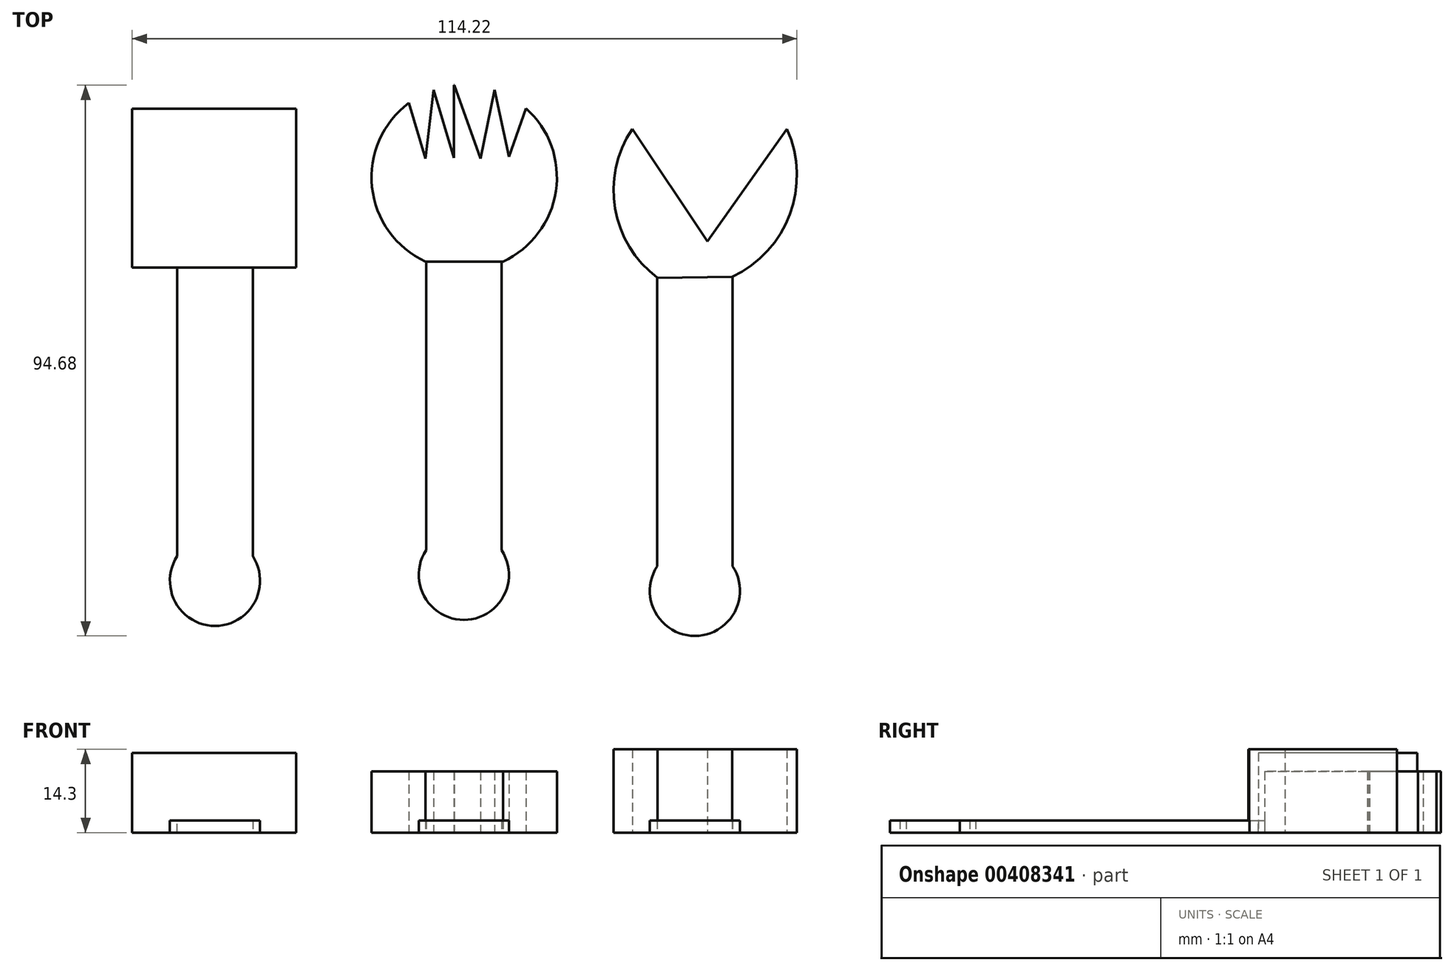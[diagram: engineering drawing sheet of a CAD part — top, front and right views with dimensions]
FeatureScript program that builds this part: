
annotation { "Feature Type Name" : "Feature", "Feature Type Description" : "" }
export const myFeature = defineFeature(function(context is Context, id is Id, definition is map)
    precondition{}
    {
        {
            var Q0;
            Q0=qCreatedBy(makeId("Top.planeOp"),FACE);
            var sketch = newSketch(context, id + "F0", { "sketchPlane" : qUnion([Q0])});
            skArc(sketch, "E0", {"start": v(-4.8, -17.78) * mm, "mid": v(1.69, -29.76) * mm, "end": v(8.18, -17.78) * mm});
            skLineSegment(sketch, "E1", {"start": v(-4.8, -17.78) * mm, "end": v(-4.8, 32) * mm});
            skLineSegment(sketch, "E2", {"start": v(8.18, -17.78) * mm, "end": v(8.18, 32) * mm});
            skLineSegment(sketch, "E3", {"start": v(-4.8, 32) * mm, "end": v(8.18, 32) * mm});
            skSolve(sketch);
        }
        {
            var Q0;
            Q0 = qSketchRegion(id + "F0", true);
            extrude(context, id + "F1", {"entities" : qUnion([Q0]), "depth" : 2.1 * mm});
        }
        {
            var Q0;
            Q0=qCreatedBy(makeId("Top.planeOp"),FACE);
            var sketch = newSketch(context, id + "F2", { "sketchPlane" : qUnion([Q0])});
            skArc(sketch, "E4", {"start": v(-47.56, -18.81) * mm, "mid": v(-41.07, -30.8) * mm, "end": v(-34.58, -18.81) * mm});
            skLineSegment(sketch, "E5", {"start": v(-47.56, -18.81) * mm, "end": v(-47.56, 30.97) * mm});
            skLineSegment(sketch, "E6", {"start": v(-34.58, -18.81) * mm, "end": v(-34.58, 30.97) * mm});
            skLineSegment(sketch, "E7", {"start": v(-47.56, 30.97) * mm, "end": v(-34.58, 30.97) * mm});
            skSolve(sketch);
        }
        {
            var Q0;
            Q0 = qSketchRegion(id + "F2", true);
            extrude(context, id + "F3", {"entities" : qUnion([Q0]), "depth" : 2.1 * mm});
        }
        {
            var Q0;
            Q0=qCreatedBy(makeId("Top.planeOp"),FACE);
            var sketch = newSketch(context, id + "F4", { "sketchPlane" : qUnion([Q0])});
            skArc(sketch, "E8", {"start": v(34.91, -20.54) * mm, "mid": v(41.4, -32.52) * mm, "end": v(47.89, -20.54) * mm});
            skLineSegment(sketch, "E9", {"start": v(34.91, -20.54) * mm, "end": v(34.91, 29.25) * mm});
            skLineSegment(sketch, "E10", {"start": v(47.89, -20.54) * mm, "end": v(47.89, 29.25) * mm});
            skLineSegment(sketch, "E11", {"start": v(34.91, 29.25) * mm, "end": v(47.89, 29.25) * mm});
            skSolve(sketch);
        }
        {
            var Q0;
            Q0=qCreatedBy(makeId("Top.planeOp"),FACE);
            var sketch = newSketch(context, id + "F5", { "sketchPlane" : qUnion([Q0])});
            skArc(sketch, "E12", {"start": v(8.4, 31.85) * mm, "mid": v(1.75, 62.26) * mm, "end": v(-4.9, 31.85) * mm});
            skLineSegment(sketch, "E13", {"start": v(12.37, 58.2) * mm, "end": v(9.45, 49.88) * mm});
            skLineSegment(sketch, "E14", {"start": v(9.45, 49.88) * mm, "end": v(6.98, 61.37) * mm});
            skLineSegment(sketch, "E15", {"start": v(6.98, 61.37) * mm, "end": v(4.55, 49.53) * mm});
            skLineSegment(sketch, "E16", {"start": v(4.55, 49.53) * mm, "end": v(0, 62.26) * mm});
            skPoint(sketch, "E16.endSnap0", {"position": v(1.75, 62.26) * mm});
            skLineSegment(sketch, "E17", {"start": v(0, 62.26) * mm, "end": v(0, 49.7) * mm});
            skLineSegment(sketch, "E18", {"start": v(0, 49.7) * mm, "end": v(-3.48, 61.37) * mm});
            skLineSegment(sketch, "E19", {"start": v(-3.48, 61.37) * mm, "end": v(-4.9, 49.53) * mm});
            skLineSegment(sketch, "E20", {"start": v(-4.9, 49.53) * mm, "end": v(-7.76, 59.1) * mm});
            skLineSegment(sketch, "E21", {"start": v(-4.9, 31.85) * mm, "end": v(8.4, 31.85) * mm});
            skSolve(sketch);
        }
        {
            var Q0;
            Q0=qCreatedBy(makeId("Top.planeOp"),FACE);
            var sketch = newSketch(context, id + "F6", { "sketchPlane" : qUnion([Q0])});
            skLineSegment(sketch, "E22.bottom", {"start": v(-27.13, 58.1) * mm, "end": v(-55.3, 58.1) * mm});
            skLineSegment(sketch, "E22.top", {"start": v(-27.13, 30.8) * mm, "end": v(-55.3, 30.8) * mm});
            skLineSegment(sketch, "E22.left", {"start": v(-27.13, 58.1) * mm, "end": v(-27.13, 30.8) * mm});
            skLineSegment(sketch, "E22.right", {"start": v(-55.3, 58.1) * mm, "end": v(-55.3, 30.8) * mm});
            skSolve(sketch);
        }
        {
            var Q0;
            {var subQ8=sQuery(id+"F5.wireOp",EDGE,"E13");Q0=makeQuery(id+"F5.imprint","IMPRINT",FACE,{"disambiguationData":[TD([[makeQuery(id+"F5.imprint","IMPRINT",EDGE,{"derivedFrom":subQ8}),1.0]])]});}
            extrude(context, id + "F7", {"entities" : qUnion([Q0]), "operationType" : NewBodyOperationType.ADD, "depth" : 10.5 * mm});
        }
        {
            var Q0;
            Q0 = qSketchRegion(id + "F6", true);
            extrude(context, id + "F8", {"entities" : qUnion([Q0]), "operationType" : NewBodyOperationType.ADD, "depth" : 13.7 * mm});
        }
        {
            var Q0;
            Q0=makeQuery(id+"F4.imprint","IMPRINT",FACE,{"disambiguationData":[TD([[makeQuery(id+"F4.imprint","IMPRINT",EDGE,{"derivedFrom":sQuery(id+"F4.wireOp",EDGE,"E8")}),1.0]])]});
            extrude(context, id + "F9", {"entities" : qUnion([Q0]), "depth" : 2.1 * mm});
        }
        {
            var Q0;
            Q0=qCreatedBy(makeId("Top.planeOp"),FACE);
            var sketch = newSketch(context, id + "F10", { "sketchPlane" : qUnion([Q0])});
            skArc(sketch, "E23", {"start": v(30.63, 54.6) * mm, "mid": v(27.69, 40.95) * mm, "end": v(35, 29.05) * mm});
            skArc(sketch, "E24", {"start": v(47.78, 29.23) * mm, "mid": v(57.7, 39.97) * mm, "end": v(57.23, 54.6) * mm});
            skLineSegment(sketch, "E25", {"start": v(57.23, 54.6) * mm, "end": v(43.58, 35.35) * mm});
            skLineSegment(sketch, "E26", {"start": v(43.58, 35.35) * mm, "end": v(30.63, 54.6) * mm});
            skLineSegment(sketch, "E27", {"start": v(35, 29.05) * mm, "end": v(47.78, 29.23) * mm});
            skSolve(sketch);
        }
        {
            var Q0;
            Q0 = qSketchRegion(id + "F10", true);
            extrude(context, id + "F11", {"entities" : qUnion([Q0]), "operationType" : NewBodyOperationType.ADD, "depth" : 14.3 * mm});
        }
    });
